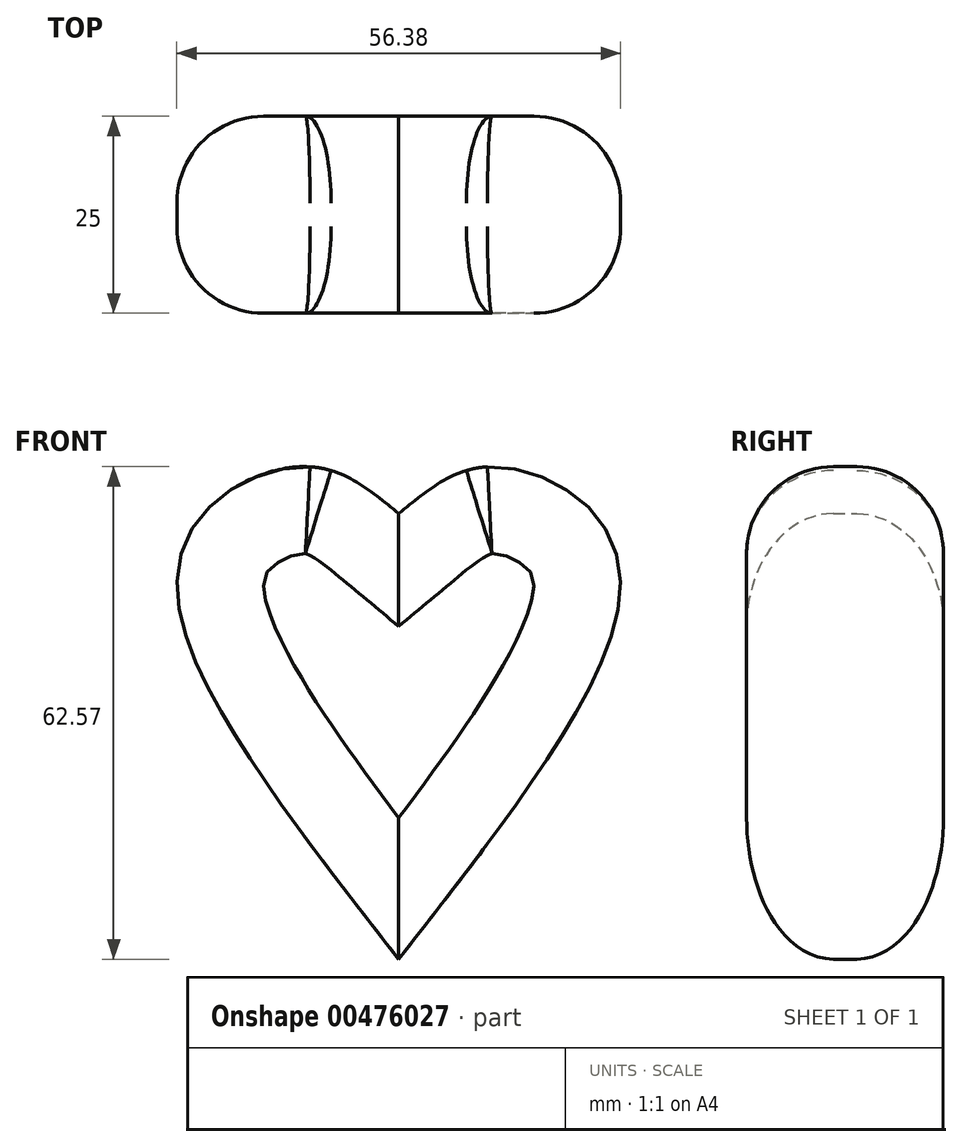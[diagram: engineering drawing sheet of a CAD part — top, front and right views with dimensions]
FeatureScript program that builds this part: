
annotation { "Feature Type Name" : "Feature", "Feature Type Description" : "" }
export const myFeature = defineFeature(function(context is Context, id is Id, definition is map)
    precondition{}
    {
        {
            var Q0;
            Q0=qCreatedBy(makeId("Front.planeOp"),FACE);
            var sketch = newSketch(context, id + "F0", { "sketchPlane" : qUnion([Q0])});
            skFitSpline(sketch, "E0", {"points": [v(0, 0) * mm, v(-27.91, 44.57) * mm, v(-23.29, 58.14) * mm, v(-10.33, 62.46) * mm, v(0, 56.6) * mm], "startDerivative": vector(-97.65, 124.95) * mm, "endDerivative": vector(50.4, -42) * mm});
            skFitSpline(sketch, "E1.MirrorCS", {"points": [v(0, 0) * mm, v(27.91, 44.57) * mm, v(23.29, 58.14) * mm, v(10.33, 62.46) * mm, v(0, 56.6) * mm], "startDerivative": vector(97.65, 124.95) * mm, "endDerivative": vector(-50.4, -42) * mm});
            skSolve(sketch);
        }
        {
            var Q0;
            Q0 = qSketchRegion(id + "F0", true);
            extrude(context, id + "F1", {"entities" : qUnion([Q0]), "depth" : 25 * mm});
        }
        {
            var Q0;
            Q0=makeQuery(id+"F1.opExtrude","CAP_EDGE",EDGE,{"disambiguationData":[OSD([sQuery(id+"F0.wireOp",EDGE,"E0")])],"isStart":false});
            var Q1;
            Q1=makeQuery(id+"F1.opExtrude","CAP_EDGE",EDGE,{"disambiguationData":[OSD([sQuery(id+"F0.wireOp",EDGE,"E1.MirrorCS")])],"isStart":false});
            var Q2;
            Q2=makeQuery(id+"F1.opExtrude","CAP_EDGE",EDGE,{"disambiguationData":[OSD([sQuery(id+"F0.wireOp",EDGE,"E1.MirrorCS")])],"isStart":true});
            var Q3;
            Q3=makeQuery(id+"F1.opExtrude","CAP_EDGE",EDGE,{"disambiguationData":[OSD([sQuery(id+"F0.wireOp",EDGE,"E0")])],"isStart":true});
            fillet(context, id + "F2", {"entities" : qUnion([Q0, Q1, Q2, Q3]), "radius" : 11 * mm, "tangentPropagation" : true, "allowEdgeOverflow" : false});
        }
    });
